# Revit family: A35-S400 BL 2200 HF 830_Unhosted
name_source: partatom
category: Lighting Fixtures
revit_build: Autodesk Revit 2016 (Build: 20151007_0715(x64)
units: mm (PartAtom-declared; Revit-internal decimal feet)

## family parameters
Always vertical = Yes
Cut with Voids When Loaded = No
Light Source = Yes
OmniClass Number = 23.80.70.00
OmniClass Title = Lighting
Part Type = Normal
Room Calculation Point = No
Round Connector Dimension = Use Diameter
Shared = No
Work Plane-Based = No

## types (1)
- A35-S400 BL 2200 HF 830_Unhosted
    #Ballast = 1
    Apparent Load = 20 VA
    ArticleNumber = A35539502
    Body Material and Colour = Default
    Color Filter = 16777215
    Description = A35-S400 BL 2200 HF 830
    Diameter = 400 mm
    Dimming Lamp Color Temperature Shift = Incandescent Lamp Curve
    Distance2 = 156 mm
    EANNo = 4741145395021
    Emit Shape Visible in Rendering = Yes
    Emit from Circle Diameter = 400 mm
    Expired = 0
    Frequency = 50 Hz
    FrequencyMax = 60 Hz
    Glamox Category = Architectural
    Glamox Family = A35-S
    Glamox Mounting = Surface
    GlobalTradeItemNumber = 4741145395021
    Height = 85 mm  [stored 0.278871 ft]
    IFC Classification = Light Fixture
    IPClass = 54
    IP_Code = 54
    Lamp = LED
    LightFixtureMountingType = SURFACE
    LightFixturePlacingType = CEILING
    LumDiameter = 400 mm
    MFArtNo = A35539502
    MaintenanceFactor = 0
    Manufacturer = Glamox
    Maximum TA = 25
    ModelLabel = A35-S400 BL 2200 HF 830
    ModelReference = A35-S
    NominalFrequencyRange = 50 Hz
    Number of Poles = 1
    Optic = OP
    Photometric Web File = A35-S400-2200-830.ies
    Power Factor = 0.98
    PowerFactor = 98.00%
    Radius = 200 mm
    RatedVoltage = 220 V
    Specification = False
    Termination = 5x2x2,5 PI
    Tilt Angle = 90.00°
    Total Load = 20 W
    TotalWattage = 20 W
    TypeOfBallast = HF = High frequency
    URL Denmark = http://glamox.com
    URL Estonia = http://glamox.com
    URL Finland = http://glamox.com
    URL Germany = http://glamox.com
    URL Ireland = http://glamox.com
    URL Norway = http://glamox.com
    URL Other = http://glamox.com
    URL Russia = http://glamox.com
    URL Sweden = http://glamox.com
    URL UK = http://glamox.com
    UpdateDate = 25.01.2021 10:33:26
    Voltage = 220 V
    VoltageMax = 240 V

note: [stored X ft] marks values corroborated as IEEE doubles in the binary element streams (Revit-internal decimal feet)

## geometry (parser evidence)
native form markers: Blend x8, Sweep x2
no freeform markers — native parametric forms only
